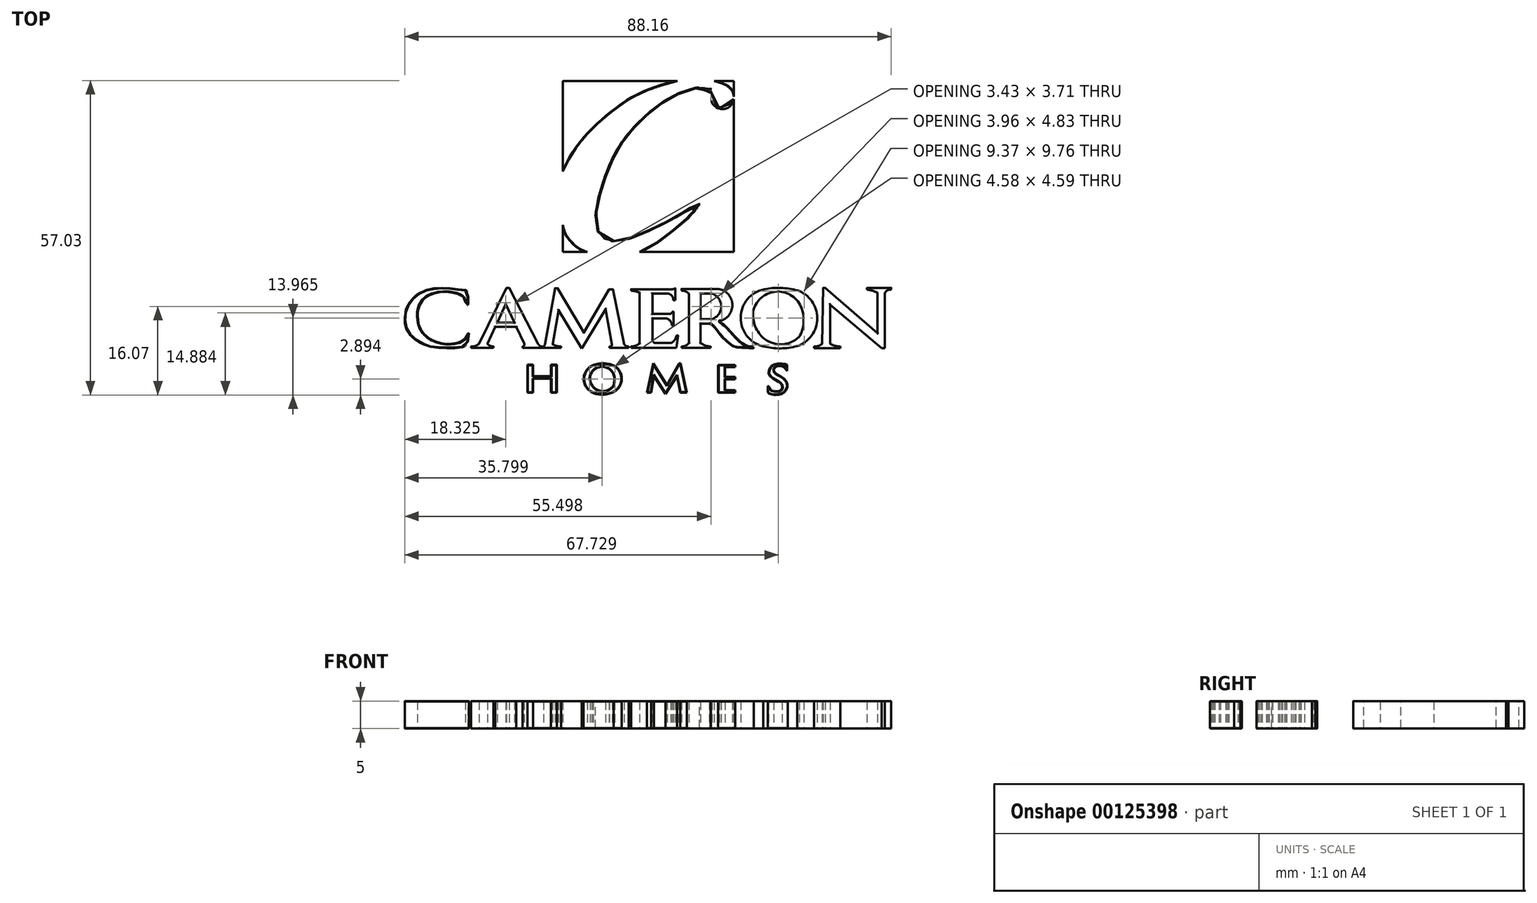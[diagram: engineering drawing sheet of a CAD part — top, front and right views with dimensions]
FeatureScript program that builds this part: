
annotation { "Feature Type Name" : "Feature", "Feature Type Description" : "" }
export const myFeature = defineFeature(function(context is Context, id is Id, definition is map)
    precondition{}
    {
        {
            var Q0;
            Q0=qCreatedBy(makeId("Top.planeOp"),FACE);
            var sketch = newSketch(context, id + "F0", { "sketchPlane" : qUnion([Q0])});
            skLineSegment(sketch, "E0.bottom", {"start": v(-14.52, 26.91) * mm, "end": v(6.23, 26.91) * mm});
            skLineSegment(sketch, "E0.top", {"start": v(-14.52, -4.09) * mm, "end": v(-10.07, -4.09) * mm});
            skLineSegment(sketch, "E0.left", {"start": v(-14.52, 26.91) * mm, "end": v(-14.52, 10.55) * mm});
            skLineSegment(sketch, "E0.right", {"start": v(16.48, 26.91) * mm, "end": v(16.48, -4.09) * mm});
            skFitSpline(sketch, "E1", {"points": [v(-14.52, 10.55) * mm, v(-12.8, 13.8) * mm, v(-10.54, 16.79) * mm, v(-7.6, 19.72) * mm, v(-4.25, 22.4) * mm, v(-1.84, 23.97) * mm, v(0.84, 25.23) * mm, v(3.82, 26.27) * mm, v(6.23, 26.91) * mm], "startDerivative": vector(12.47, 25.45) * mm, "endDerivative": vector(21.85, 5.4) * mm});
            skFitSpline(sketch, "E2", {"points": [v(-14.52, 0.8) * mm, v(-13.95, -0.93) * mm, v(-12.74, -2.45) * mm, v(-11.64, -3.4) * mm, v(-10.07, -4.09) * mm], "startDerivative": vector(1.63, -6.9) * mm, "endDerivative": vector(6.75, -2.5) * mm});
            skFitSpline(sketch, "E3", {"points": [v(-0.63, -4.09) * mm, v(1.88, -2.77) * mm, v(4.5, -0.88) * mm, v(7.18, 1.27) * mm, v(9.12, 3.1) * mm, v(9.91, 3.98) * mm, v(10.2, 4.54) * mm, v(9.82, 4.57) * mm, v(8.32, 3.65) * mm, v(3.94, 1.1) * mm, v(-1.34, -1.28) * mm, v(-4.31, -2.14) * mm, v(-6.9, -1.81) * mm, v(-8.23, -0.28) * mm, v(-8.56, 3.08) * mm, v(-6.57, 10.42) * mm, v(-3.28, 16.62) * mm, v(2, 21.93) * mm, v(6.58, 24.77) * mm, v(10.85, 25.92) * mm, v(12.15, 25.85) * mm, v(12.46, 25.26) * mm, v(12.36, 23.5) * mm, v(12.99, 22.35) * mm, v(14.38, 21.83) * mm, v(15.71, 22.28) * mm, v(16.48, 23.61) * mm, v(16, 25.33) * mm, v(14.84, 26.24) * mm, v(12.92, 26.91) * mm], "startDerivative": vector(70.33, 33.7) * mm, "endDerivative": vector(-67.14, 20.33) * mm});
            skLineSegment(sketch, "E4.trimOffspring", {"start": v(12.92, 26.91) * mm, "end": v(16.48, 26.91) * mm});
            skLineSegment(sketch, "E5.trimOffspring", {"start": v(-14.52, 0.8) * mm, "end": v(-14.52, -4.09) * mm});
            skLineSegment(sketch, "E6.trimOffspring", {"start": v(-0.63, -4.09) * mm, "end": v(16.48, -4.09) * mm});
            skLineSegment(sketch, "E7.bottom", {"start": v(-43.46, -10.36) * mm, "end": v(45.19, -10.36) * mm, "construction": true});
            skLineSegment(sketch, "E7.top", {"start": v(-43.46, -21.79) * mm, "end": v(45.19, -21.79) * mm, "construction": true});
            skLineSegment(sketch, "E7.left", {"start": v(-43.46, -10.36) * mm, "end": v(-43.46, -21.79) * mm, "construction": true});
            skLineSegment(sketch, "E7.right", {"start": v(45.19, -10.36) * mm, "end": v(45.19, -21.79) * mm, "construction": true});
            skPoint(sketch, "E8.23.internal.snap0", {"position": v(-43.46, -16.07) * mm});
            skFitSpline(sketch, "E8", {"points": [v(-33.2, -10.89) * mm, v(-34.84, -10.69) * mm, v(-37.55, -10.64) * mm, v(-40.62, -11.6) * mm, v(-42.6, -13.73) * mm, v(-43.1, -15.32) * mm, v(-43.1, -17.3) * mm, v(-42.36, -18.9) * mm, v(-40.77, -20.32) * mm, v(-38.83, -21.2) * mm, v(-37.55, -21.44) * mm, v(-33.12, -21.47) * mm, v(-32.6, -21.36) * mm, v(-32, -21) * mm, v(-31.53, -19.02) * mm, v(-31.62, -18.87) * mm, v(-31.95, -19.33) * mm, v(-32.42, -19.99) * mm, v(-33.25, -20.45) * mm, v(-34.97, -20.76) * mm, v(-36.91, -20.56) * mm, v(-39.25, -19.4) * mm, v(-40.5, -17.7) * mm, v(-40.81, -16.07) * mm, v(-40.77, -14.52) * mm, v(-39.93, -12.8) * mm, v(-38.57, -11.83) * mm, v(-36.65, -11.37) * mm, v(-34.8, -11.42) * mm, v(-33.32, -11.77) * mm, v(-32.53, -12.28) * mm, v(-32.17, -12.91) * mm, v(-32.1, -13.77) * mm, v(-31.78, -13.84) * mm, v(-31.67, -12.96) * mm, v(-31.69, -11.77) * mm, v(-31.78, -11.13) * mm, v(-33.2, -10.89) * mm]});
            skLineSegment(sketch, "E9", {"start": v(-29.73, -20.74) * mm, "end": v(-24.72, -10.6) * mm});
            skLineSegment(sketch, "E10", {"start": v(-24.72, -10.6) * mm, "end": v(-24.26, -10.6) * mm});
            skLineSegment(sketch, "E11", {"start": v(-24.26, -10.6) * mm, "end": v(-19.04, -20.74) * mm});
            skLineSegment(sketch, "E12", {"start": v(-21.54, -20.74) * mm, "end": v(-24.86, -13.52) * mm});
            skLineSegment(sketch, "E13", {"start": v(-24.86, -13.52) * mm, "end": v(-28.2, -20.7) * mm});
            skLineSegment(sketch, "E14", {"start": v(-26.42, -16.9) * mm, "end": v(-23.3, -16.9) * mm});
            skLineSegment(sketch, "E15", {"start": v(-26.78, -17.66) * mm, "end": v(-22.95, -17.66) * mm});
            skLineSegment(sketch, "E16", {"start": v(-31.15, -21.24) * mm, "end": v(-31.15, -21.49) * mm});
            skLineSegment(sketch, "E17", {"start": v(-31.15, -21.49) * mm, "end": v(-27.07, -21.49) * mm});
            skLineSegment(sketch, "E18", {"start": v(-27.07, -21.49) * mm, "end": v(-27.07, -21.24) * mm});
            skLineSegment(sketch, "E19", {"start": v(-21.83, -21.24) * mm, "end": v(-21.83, -21.49) * mm});
            skLineSegment(sketch, "E20", {"start": v(-21.83, -21.49) * mm, "end": v(-18, -21.49) * mm});
            skLineSegment(sketch, "E21", {"start": v(-18, -21.49) * mm, "end": v(-18, -21.24) * mm});
            skArc(sketch, "E22", {"start": v(-31.15, -21.24) * mm, "mid": v(-30.38, -21.14) * mm, "end": v(-29.73, -20.74) * mm});
            skArc(sketch, "E23", {"start": v(-28.2, -20.7) * mm, "mid": v(-27.7, -21.1) * mm, "end": v(-27.07, -21.24) * mm});
            skArc(sketch, "E24", {"start": v(-21.83, -21.24) * mm, "mid": v(-21.55, -21.06) * mm, "end": v(-21.54, -20.74) * mm});
            skArc(sketch, "E25", {"start": v(-19.04, -20.74) * mm, "mid": v(-18.6, -21.16) * mm, "end": v(-18, -21.24) * mm});
            skLineSegment(sketch, "E26", {"start": v(-17.78, -20.8) * mm, "end": v(-15.93, -10.65) * mm});
            skLineSegment(sketch, "E27", {"start": v(-15.93, -10.65) * mm, "end": v(-15.45, -10.65) * mm});
            skLineSegment(sketch, "E28", {"start": v(-15.45, -10.65) * mm, "end": v(-10.72, -18.68) * mm});
            skLineSegment(sketch, "E29", {"start": v(-10.72, -18.68) * mm, "end": v(-6.12, -10.86) * mm});
            skLineSegment(sketch, "E30", {"start": v(-6.12, -10.86) * mm, "end": v(-5.47, -10.86) * mm});
            skLineSegment(sketch, "E31", {"start": v(-5.47, -10.86) * mm, "end": v(-3.4, -20.8) * mm});
            skLineSegment(sketch, "E32", {"start": v(-16.38, -20.8) * mm, "end": v(-15.3, -14.7) * mm});
            skLineSegment(sketch, "E33", {"start": v(-15.3, -14.7) * mm, "end": v(-11.1, -21.58) * mm});
            skLineSegment(sketch, "E34", {"start": v(-11.1, -21.58) * mm, "end": v(-6.78, -14.48) * mm});
            skLineSegment(sketch, "E35", {"start": v(-6.78, -14.48) * mm, "end": v(-5.61, -20.8) * mm});
            skLineSegment(sketch, "E36", {"start": v(-18, -21.49) * mm, "end": v(-14.86, -21.49) * mm});
            skLineSegment(sketch, "E37", {"start": v(-14.86, -21.49) * mm, "end": v(-14.86, -21.24) * mm});
            skLineSegment(sketch, "E38", {"start": v(-6.05, -21.49) * mm, "end": v(-2.6, -21.49) * mm});
            skLineSegment(sketch, "E39", {"start": v(-2.6, -21.49) * mm, "end": v(-2.6, -21.24) * mm});
            skLineSegment(sketch, "E40", {"start": v(-6.05, -21.49) * mm, "end": v(-6.05, -21.24) * mm});
            skArc(sketch, "E41", {"start": v(-18, -21.24) * mm, "mid": v(-17.86, -21.04) * mm, "end": v(-17.78, -20.8) * mm});
            skArc(sketch, "E42", {"start": v(-16.38, -20.8) * mm, "mid": v(-15.65, -21.13) * mm, "end": v(-14.86, -21.24) * mm});
            skArc(sketch, "E43", {"start": v(-6.05, -21.24) * mm, "mid": v(-5.72, -21.14) * mm, "end": v(-5.61, -20.8) * mm});
            skArc(sketch, "E44", {"start": v(-3.4, -20.8) * mm, "mid": v(-3.05, -21.13) * mm, "end": v(-2.6, -21.24) * mm});
            skLineSegment(sketch, "E45", {"start": v(-2.16, -10.85) * mm, "end": v(5.22, -10.85) * mm});
            skLineSegment(sketch, "E46", {"start": v(-0.62, -11.48) * mm, "end": v(-0.62, -20.66) * mm});
            skLineSegment(sketch, "E47", {"start": v(4.35, -11.62) * mm, "end": v(1.71, -11.62) * mm});
            skLineSegment(sketch, "E48", {"start": v(1.71, -11.62) * mm, "end": v(1.71, -15.31) * mm});
            skLineSegment(sketch, "E49", {"start": v(1.71, -15.31) * mm, "end": v(4.87, -15.31) * mm});
            skLineSegment(sketch, "E50", {"start": v(4.4, -16.15) * mm, "end": v(1.71, -16.15) * mm});
            skLineSegment(sketch, "E51", {"start": v(1.71, -16.15) * mm, "end": v(1.71, -19.82) * mm});
            skLineSegment(sketch, "E52", {"start": v(2.32, -20.61) * mm, "end": v(5.03, -20.61) * mm});
            skLineSegment(sketch, "E53", {"start": v(5.85, -10.66) * mm, "end": v(5.85, -12.86) * mm});
            skLineSegment(sketch, "E54", {"start": v(5.54, -14.96) * mm, "end": v(5.54, -17.39) * mm});
            skLineSegment(sketch, "E55", {"start": v(6.38, -19.28) * mm, "end": v(6.07, -21.49) * mm});
            skLineSegment(sketch, "E56", {"start": v(6.07, -21.49) * mm, "end": v(-2.16, -21.49) * mm});
            skLineSegment(sketch, "E57", {"start": v(-2.16, -21.49) * mm, "end": v(-2.16, -21.24) * mm});
            skLineSegment(sketch, "E58", {"start": v(-2.16, -10.85) * mm, "end": v(-2.16, -11.13) * mm});
            skLineSegment(sketch, "E59", {"start": v(5.85, -12.86) * mm, "end": v(5.5, -12.86) * mm});
            skLineSegment(sketch, "E60", {"start": v(5.54, -14.96) * mm, "end": v(5.3, -14.96) * mm});
            skLineSegment(sketch, "E61", {"start": v(5.54, -17.39) * mm, "end": v(5.25, -17.39) * mm});
            skLineSegment(sketch, "E62", {"start": v(6.38, -19.28) * mm, "end": v(6.05, -19.28) * mm});
            skArc(sketch, "E63", {"start": v(-0.62, -11.48) * mm, "mid": v(-1.37, -11.21) * mm, "end": v(-2.16, -11.13) * mm});
            skArc(sketch, "E64", {"start": v(-2.16, -21.24) * mm, "mid": v(-1.34, -21.09) * mm, "end": v(-0.62, -20.66) * mm});
            skArc(sketch, "E65", {"start": v(5.5, -12.86) * mm, "mid": v(5.2, -12) * mm, "end": v(4.35, -11.62) * mm});
            skArc(sketch, "E66", {"start": v(5.25, -17.39) * mm, "mid": v(5, -16.65) * mm, "end": v(4.4, -16.15) * mm});
            skArc(sketch, "E67", {"start": v(5.03, -20.61) * mm, "mid": v(5.71, -20.08) * mm, "end": v(6.05, -19.28) * mm});
            skArc(sketch, "E68", {"start": v(1.71, -19.82) * mm, "mid": v(1.82, -20.36) * mm, "end": v(2.32, -20.61) * mm});
            skArc(sketch, "E69", {"start": v(4.87, -15.31) * mm, "mid": v(5.14, -15.21) * mm, "end": v(5.3, -14.96) * mm});
            skArc(sketch, "E70", {"start": v(5.22, -10.85) * mm, "mid": v(5.55, -10.8) * mm, "end": v(5.85, -10.66) * mm});
            skLineSegment(sketch, "E71", {"start": v(6.97, -10.8) * mm, "end": v(13.74, -10.8) * mm});
            skPoint(sketch, "E71.startSnap0", {"position": v(5.55, -10.8) * mm});
            skLineSegment(sketch, "E72", {"start": v(10.43, -11.64) * mm, "end": v(10.43, -16.26) * mm});
            skLineSegment(sketch, "E73", {"start": v(10.43, -16.26) * mm, "end": v(12.5, -16.26) * mm});
            skLineSegment(sketch, "E74", {"start": v(8.36, -11.7) * mm, "end": v(8.36, -20.58) * mm});
            skLineSegment(sketch, "E75", {"start": v(12.04, -17.1) * mm, "end": v(10.43, -17.1) * mm});
            skLineSegment(sketch, "E76", {"start": v(10.43, -17.1) * mm, "end": v(10.43, -20.58) * mm});
            skLineSegment(sketch, "E77", {"start": v(7.01, -21.49) * mm, "end": v(12.26, -21.49) * mm});
            skLineSegment(sketch, "E78", {"start": v(12.26, -21.49) * mm, "end": v(12.26, -21.24) * mm});
            skLineSegment(sketch, "E79", {"start": v(7.01, -21.49) * mm, "end": v(7.01, -21.24) * mm});
            skArc(sketch, "E80", {"start": v(7.01, -21.24) * mm, "mid": v(7.76, -21.07) * mm, "end": v(8.36, -20.58) * mm});
            skArc(sketch, "E81", {"start": v(10.43, -20.58) * mm, "mid": v(11.3, -21.05) * mm, "end": v(12.26, -21.24) * mm});
            skLineSegment(sketch, "E82", {"start": v(6.97, -10.8) * mm, "end": v(6.97, -11.1) * mm});
            skArc(sketch, "E83", {"start": v(8.36, -11.7) * mm, "mid": v(7.74, -11.23) * mm, "end": v(6.97, -11.1) * mm});
            skLineSegment(sketch, "E84", {"start": v(10.43, -11.64) * mm, "end": v(12.5, -11.64) * mm});
            skArc(sketch, "E85", {"start": v(12.5, -16.26) * mm, "mid": v(14.19, -13.95) * mm, "end": v(12.5, -11.64) * mm});
            skArc(sketch, "E86", {"start": v(14.19, -16.53) * mm, "mid": v(16.2, -13.5) * mm, "end": v(13.74, -10.8) * mm});
            skPoint(sketch, "E86.startSnap0", {"position": v(14.19, -13.95) * mm});
            skFitSpline(sketch, "E87", {"points": [v(12.04, -17.1) * mm, v(12.53, -17.33) * mm, v(14.14, -19.28) * mm, v(15.87, -20.92) * mm, v(16.89, -21.36) * mm, v(19.98, -21.53) * mm, v(20.07, -21.51) * mm, v(19.9, -21.27) * mm, v(19.44, -21.22) * mm, v(17.87, -20.52) * mm, v(15.92, -18.58) * mm, v(14.4, -17.1) * mm, v(13.83, -16.63) * mm, v(14.19, -16.53) * mm], "startDerivative": vector(8.71, -2.21) * mm, "endDerivative": vector(12, 1.45) * mm});
            skArc(sketch, "E88", {"start": v(27.94, -21.15) * mm, "mid": v(31.58, -16.12) * mm, "end": v(27.99, -11.06) * mm});
            skArc(sketch, "E89", {"start": v(21.93, -10.86) * mm, "mid": v(17.7, -15.98) * mm, "end": v(21.8, -21.2) * mm});
            skArc(sketch, "E90", {"start": v(27.99, -11.06) * mm, "mid": v(24.97, -10.6) * mm, "end": v(21.93, -10.86) * mm});
            skArc(sketch, "E91", {"start": v(21.8, -21.2) * mm, "mid": v(24.87, -21.57) * mm, "end": v(27.94, -21.15) * mm});
            skArc(sketch, "E92", {"start": v(28.76, -14.32) * mm, "mid": v(24.28, -11.27) * mm, "end": v(20.02, -14.62) * mm});
            skArc(sketch, "E93", {"start": v(21.68, -19.57) * mm, "mid": v(25.03, -20.84) * mm, "end": v(28.33, -19.47) * mm});
            skArc(sketch, "E94", {"start": v(28.33, -19.47) * mm, "mid": v(29.1, -16.94) * mm, "end": v(28.76, -14.32) * mm});
            skArc(sketch, "E95", {"start": v(20.02, -14.62) * mm, "mid": v(20.24, -17.3) * mm, "end": v(21.68, -19.57) * mm});
            skLineSegment(sketch, "E96", {"start": v(32.45, -20.73) * mm, "end": v(32.66, -10.58) * mm});
            skLineSegment(sketch, "E97", {"start": v(32.66, -10.58) * mm, "end": v(33.06, -10.59) * mm});
            skLineSegment(sketch, "E98", {"start": v(33.06, -10.59) * mm, "end": v(42.5, -18.77) * mm});
            skLineSegment(sketch, "E99", {"start": v(42.5, -18.77) * mm, "end": v(42.5, -11.53) * mm});
            skLineSegment(sketch, "E100", {"start": v(43.85, -11.53) * mm, "end": v(43.85, -21.56) * mm});
            skLineSegment(sketch, "E101", {"start": v(43.85, -21.56) * mm, "end": v(43.23, -21.56) * mm});
            skLineSegment(sketch, "E102", {"start": v(43.23, -21.56) * mm, "end": v(33.93, -13.64) * mm});
            skLineSegment(sketch, "E103", {"start": v(33.93, -13.64) * mm, "end": v(33.93, -20.73) * mm});
            skLineSegment(sketch, "E104", {"start": v(31.03, -21.24) * mm, "end": v(31.03, -21.51) * mm});
            skLineSegment(sketch, "E105", {"start": v(31.03, -21.51) * mm, "end": v(35.76, -21.51) * mm});
            skLineSegment(sketch, "E106", {"start": v(35.76, -21.51) * mm, "end": v(35.76, -21.24) * mm});
            skLineSegment(sketch, "E107", {"start": v(40.6, -10.59) * mm, "end": v(44.97, -10.59) * mm});
            skLineSegment(sketch, "E108", {"start": v(44.97, -10.59) * mm, "end": v(44.97, -10.95) * mm});
            skLineSegment(sketch, "E109", {"start": v(40.6, -10.59) * mm, "end": v(40.6, -10.95) * mm});
            skArc(sketch, "E110", {"start": v(31.03, -21.24) * mm, "mid": v(31.8, -21.13) * mm, "end": v(32.45, -20.73) * mm});
            skArc(sketch, "E111", {"start": v(33.93, -20.73) * mm, "mid": v(34.81, -21.1) * mm, "end": v(35.76, -21.24) * mm});
            skArc(sketch, "E112", {"start": v(42.5, -11.53) * mm, "mid": v(41.6, -11.1) * mm, "end": v(40.6, -10.95) * mm});
            skArc(sketch, "E113", {"start": v(44.97, -10.95) * mm, "mid": v(44.31, -11.04) * mm, "end": v(43.85, -11.53) * mm});
            skLineSegment(sketch, "E114.bottom", {"start": v(-20.97, -24.52) * mm, "end": v(-19.92, -24.52) * mm});
            skLineSegment(sketch, "E114.top", {"start": v(-20.97, -29.63) * mm, "end": v(-19.92, -29.63) * mm});
            skLineSegment(sketch, "E114.left", {"start": v(-20.97, -24.52) * mm, "end": v(-20.97, -29.63) * mm});
            skLineSegment(sketch, "E114.right", {"start": v(-19.92, -24.52) * mm, "end": v(-19.92, -29.63) * mm});
            skLineSegment(sketch, "E115.bottom", {"start": v(-16.67, -24.52) * mm, "end": v(-15.62, -24.52) * mm});
            skLineSegment(sketch, "E115.top", {"start": v(-16.67, -29.63) * mm, "end": v(-15.62, -29.63) * mm});
            skLineSegment(sketch, "E115.left", {"start": v(-16.67, -24.52) * mm, "end": v(-16.67, -29.63) * mm});
            skLineSegment(sketch, "E115.right", {"start": v(-15.62, -24.52) * mm, "end": v(-15.62, -29.63) * mm});
            skLineSegment(sketch, "E116.bottom", {"start": v(-19.92, -26.64) * mm, "end": v(-16.67, -26.64) * mm});
            skLineSegment(sketch, "E116.top", {"start": v(-19.92, -27.07) * mm, "end": v(-16.67, -27.07) * mm});
            skLineSegment(sketch, "E116.left", {"start": v(-19.92, -26.64) * mm, "end": v(-19.92, -27.07) * mm});
            skLineSegment(sketch, "E116.right", {"start": v(-16.67, -26.64) * mm, "end": v(-16.67, -27.07) * mm});
            skArc(sketch, "E117", {"start": v(-5.2, -27) * mm, "mid": v(-7.2, -24.93) * mm, "end": v(-9.55, -26.6) * mm});
            skArc(sketch, "E118", {"start": v(-9.28, -28.1) * mm, "mid": v(-7.34, -29.32) * mm, "end": v(-5.33, -28.23) * mm});
            skArc(sketch, "E119", {"start": v(-5.33, -28.23) * mm, "mid": v(-5.23, -27.62) * mm, "end": v(-5.2, -27) * mm});
            skArc(sketch, "E120", {"start": v(-9.55, -26.6) * mm, "mid": v(-9.55, -27.38) * mm, "end": v(-9.28, -28.1) * mm});
            skArc(sketch, "E121", {"start": v(-9.02, -24.57) * mm, "mid": v(-10.75, -27.16) * mm, "end": v(-8.93, -29.7) * mm});
            skArc(sketch, "E122", {"start": v(-5.33, -29.5) * mm, "mid": v(-3.84, -27.18) * mm, "end": v(-5.12, -24.75) * mm});
            skArc(sketch, "E123", {"start": v(-5.12, -24.75) * mm, "mid": v(-7.05, -24.29) * mm, "end": v(-9.02, -24.57) * mm});
            skArc(sketch, "E124", {"start": v(-8.93, -29.7) * mm, "mid": v(-7.1, -29.96) * mm, "end": v(-5.33, -29.5) * mm});
            skLineSegment(sketch, "E125", {"start": v(1.86, -24.29) * mm, "end": v(4.32, -28.22) * mm});
            skLineSegment(sketch, "E126", {"start": v(4.32, -28.22) * mm, "end": v(6.57, -24.29) * mm});
            skLineSegment(sketch, "E127", {"start": v(6.57, -24.29) * mm, "end": v(6.8, -24.29) * mm});
            skLineSegment(sketch, "E128", {"start": v(6.8, -24.29) * mm, "end": v(7.94, -29.57) * mm});
            skLineSegment(sketch, "E129", {"start": v(7.94, -29.57) * mm, "end": v(6.72, -29.57) * mm});
            skLineSegment(sketch, "E130", {"start": v(6.72, -29.57) * mm, "end": v(6.14, -26.64) * mm});
            skLineSegment(sketch, "E131", {"start": v(6.14, -26.64) * mm, "end": v(4.1, -29.89) * mm});
            skLineSegment(sketch, "E132", {"start": v(4.1, -29.89) * mm, "end": v(1.99, -26.59) * mm});
            skLineSegment(sketch, "E133", {"start": v(1.99, -26.59) * mm, "end": v(1.5, -29.57) * mm});
            skLineSegment(sketch, "E134", {"start": v(1.5, -29.57) * mm, "end": v(0.71, -29.57) * mm});
            skLineSegment(sketch, "E135", {"start": v(0.71, -29.57) * mm, "end": v(1.86, -24.29) * mm});
            skLineSegment(sketch, "E136.bottom", {"start": v(13.62, -24.57) * mm, "end": v(14.88, -24.57) * mm});
            skLineSegment(sketch, "E136.top", {"start": v(13.62, -29.63) * mm, "end": v(14.88, -29.63) * mm});
            skLineSegment(sketch, "E136.left", {"start": v(13.62, -24.57) * mm, "end": v(13.62, -29.63) * mm});
            skLineSegment(sketch, "E136.right", {"start": v(14.88, -24.57) * mm, "end": v(14.88, -29.63) * mm});
            skLineSegment(sketch, "E137.bottom", {"start": v(14.88, -24.57) * mm, "end": v(16.7, -24.57) * mm});
            skLineSegment(sketch, "E137.top", {"start": v(14.88, -24.97) * mm, "end": v(16.7, -24.97) * mm});
            skLineSegment(sketch, "E137.left", {"start": v(14.88, -24.57) * mm, "end": v(14.88, -24.97) * mm});
            skLineSegment(sketch, "E137.right", {"start": v(16.7, -24.57) * mm, "end": v(16.7, -24.97) * mm});
            skLineSegment(sketch, "E138.bottom", {"start": v(14.88, -26.76) * mm, "end": v(16.7, -26.76) * mm});
            skLineSegment(sketch, "E138.top", {"start": v(14.88, -27.16) * mm, "end": v(16.7, -27.16) * mm});
            skLineSegment(sketch, "E138.left", {"start": v(14.88, -26.76) * mm, "end": v(14.88, -27.16) * mm});
            skLineSegment(sketch, "E138.right", {"start": v(16.7, -26.76) * mm, "end": v(16.7, -27.16) * mm});
            skLineSegment(sketch, "E139.bottom", {"start": v(14.88, -29.63) * mm, "end": v(16.7, -29.63) * mm});
            skLineSegment(sketch, "E139.top", {"start": v(14.88, -29.15) * mm, "end": v(16.7, -29.15) * mm});
            skLineSegment(sketch, "E139.left", {"start": v(14.88, -29.63) * mm, "end": v(14.88, -29.15) * mm});
            skLineSegment(sketch, "E139.right", {"start": v(16.7, -29.63) * mm, "end": v(16.7, -29.15) * mm});
            skLineSegment(sketch, "E140", {"start": v(22.6, -28.37) * mm, "end": v(22.6, -29.54) * mm});
            skLineSegment(sketch, "E141", {"start": v(26.13, -24.51) * mm, "end": v(26.13, -25.65) * mm});
            skFitSpline(sketch, "E142", {"points": [v(26.13, -24.51) * mm, v(25.52, -24.37) * mm, v(24.08, -24.35) * mm, v(23.24, -24.8) * mm, v(22.8, -25.57) * mm, v(22.86, -26.37) * mm, v(23.68, -27.12) * mm, v(24.64, -27.69) * mm, v(25.14, -28.16) * mm, v(25.23, -28.73) * mm, v(25.05, -29.18) * mm, v(24.46, -29.34) * mm, v(23.71, -29.3) * mm, v(23.17, -29.09) * mm, v(22.9, -28.6) * mm, v(22.6, -28.37) * mm], "startDerivative": vector(-8.49, 2.6) * mm, "endDerivative": vector(-7.14, 3.76) * mm});
            skFitSpline(sketch, "E143", {"points": [v(22.6, -29.54) * mm, v(22.86, -29.78) * mm, v(23.85, -30.01) * mm, v(25, -29.88) * mm, v(25.82, -29.34) * mm, v(26.2, -28.43) * mm, v(26.02, -27.59) * mm, v(25.07, -26.67) * mm, v(24.07, -26.09) * mm, v(23.71, -25.65) * mm, v(23.77, -25.25) * mm, v(24.08, -24.9) * mm, v(24.71, -24.8) * mm, v(25.42, -24.9) * mm, v(25.76, -25.22) * mm, v(26.13, -25.65) * mm], "startDerivative": vector(4.46, -5.37) * mm, "endDerivative": vector(6.63, -7.42) * mm});
            skSolve(sketch);
        }
        {
            var Q0;
            Q0 = qSketchRegion(id + "F0", true);
            extrude(context, id + "F1", {"entities" : qUnion([Q0]), "depth" : 5 * mm});
        }
        {
            var Q0;
            Q0=makeQuery(id+"F1.opExtrude","CAP_FACE",FACE,{"disambiguationData":[OSD([sQuery(id+"F0.wireOp",EDGE,"E0.right"),sQuery(id+"F0.wireOp",EDGE,"E3"),sQuery(id+"F0.wireOp",EDGE,"E6.trimOffspring")])],"isStart":false});
            var Q1;
            Q1=makeQuery(id+"F1.opExtrude","CAP_FACE",FACE,{"disambiguationData":[OSD([sQuery(id+"F0.wireOp",EDGE,"E0.bottom"),sQuery(id+"F0.wireOp",EDGE,"E0.left"),sQuery(id+"F0.wireOp",EDGE,"E1")])],"isStart":false});
            var Q2;
            {var subQ0=sQuery(id+"F0.wireOp",EDGE,"E3");Q2=makeQuery(id+"F1.opExtrude","CAP_EDGE",EDGE,{"disambiguationData":[OSD([subQ0]),TDD([makeQuery(id+"F0.imprint","IMPRINT",EDGE,{"disambiguationData":[TD([[makeQuery(id+"F0.imprint","INTERSECT",VERTEX,{"derivedFrom":[subQ0,sQuery(id+"F0.wireOp",EDGE,"E4.trimOffspring")]}),1.0]])],"derivedFrom":subQ0})])],"isStart":false});}
            var Q3;
            Q3=makeQuery(id+"F1.opExtrude","CAP_FACE",FACE,{"disambiguationData":[OSD([sQuery(id+"F0.wireOp",EDGE,"E0.top"),sQuery(id+"F0.wireOp",EDGE,"E2"),sQuery(id+"F0.wireOp",EDGE,"E5.trimOffspring")])],"isStart":false});
            var Q4;
            Q4=makeQuery(id+"F1.opExtrude","CAP_FACE",FACE,{"disambiguationData":[OSD([sQuery(id+"F0.wireOp",EDGE,"E8")])],"isStart":false});
            var Q5;
            Q5=makeQuery(id+"F1.opExtrude","CAP_FACE",FACE,{"disambiguationData":[OSD([sQuery(id+"F0.wireOp",EDGE,"E9"),sQuery(id+"F0.wireOp",EDGE,"E10"),sQuery(id+"F0.wireOp",EDGE,"E11"),sQuery(id+"F0.wireOp",EDGE,"E12"),sQuery(id+"F0.wireOp",EDGE,"E13"),sQuery(id+"F0.wireOp",EDGE,"E14"),sQuery(id+"F0.wireOp",EDGE,"E15"),sQuery(id+"F0.wireOp",EDGE,"E16"),sQuery(id+"F0.wireOp",EDGE,"E17"),sQuery(id+"F0.wireOp",EDGE,"E18"),sQuery(id+"F0.wireOp",EDGE,"E19"),sQuery(id+"F0.wireOp",EDGE,"E20"),sQuery(id+"F0.wireOp",EDGE,"E22"),sQuery(id+"F0.wireOp",EDGE,"E23"),sQuery(id+"F0.wireOp",EDGE,"E24"),sQuery(id+"F0.wireOp",EDGE,"E25"),sQuery(id+"F0.wireOp",EDGE,"E26"),sQuery(id+"F0.wireOp",EDGE,"E27"),sQuery(id+"F0.wireOp",EDGE,"E28"),sQuery(id+"F0.wireOp",EDGE,"E29"),sQuery(id+"F0.wireOp",EDGE,"E30"),sQuery(id+"F0.wireOp",EDGE,"E31"),sQuery(id+"F0.wireOp",EDGE,"E32"),sQuery(id+"F0.wireOp",EDGE,"E33"),sQuery(id+"F0.wireOp",EDGE,"E34"),sQuery(id+"F0.wireOp",EDGE,"E35"),sQuery(id+"F0.wireOp",EDGE,"E36"),sQuery(id+"F0.wireOp",EDGE,"E37"),sQuery(id+"F0.wireOp",EDGE,"E38"),sQuery(id+"F0.wireOp",EDGE,"E39"),sQuery(id+"F0.wireOp",EDGE,"E40"),sQuery(id+"F0.wireOp",EDGE,"E41"),sQuery(id+"F0.wireOp",EDGE,"E42"),sQuery(id+"F0.wireOp",EDGE,"E43"),sQuery(id+"F0.wireOp",EDGE,"E44")])],"isStart":false});
            var Q6;
            Q6=makeQuery(id+"F1.opExtrude","CAP_FACE",FACE,{"disambiguationData":[OSD([sQuery(id+"F0.wireOp",EDGE,"E45"),sQuery(id+"F0.wireOp",EDGE,"E46"),sQuery(id+"F0.wireOp",EDGE,"E47"),sQuery(id+"F0.wireOp",EDGE,"E48"),sQuery(id+"F0.wireOp",EDGE,"E49"),sQuery(id+"F0.wireOp",EDGE,"E50"),sQuery(id+"F0.wireOp",EDGE,"E51"),sQuery(id+"F0.wireOp",EDGE,"E52"),sQuery(id+"F0.wireOp",EDGE,"E53"),sQuery(id+"F0.wireOp",EDGE,"E54"),sQuery(id+"F0.wireOp",EDGE,"E55"),sQuery(id+"F0.wireOp",EDGE,"E56"),sQuery(id+"F0.wireOp",EDGE,"E57"),sQuery(id+"F0.wireOp",EDGE,"E58"),sQuery(id+"F0.wireOp",EDGE,"E59"),sQuery(id+"F0.wireOp",EDGE,"E60"),sQuery(id+"F0.wireOp",EDGE,"E61"),sQuery(id+"F0.wireOp",EDGE,"E62"),sQuery(id+"F0.wireOp",EDGE,"E63"),sQuery(id+"F0.wireOp",EDGE,"E64"),sQuery(id+"F0.wireOp",EDGE,"E65"),sQuery(id+"F0.wireOp",EDGE,"E66"),sQuery(id+"F0.wireOp",EDGE,"E67"),sQuery(id+"F0.wireOp",EDGE,"E68"),sQuery(id+"F0.wireOp",EDGE,"E69"),sQuery(id+"F0.wireOp",EDGE,"E70")])],"isStart":false});
            var Q7;
            Q7=makeQuery(id+"F1.opExtrude","CAP_FACE",FACE,{"disambiguationData":[OSD([sQuery(id+"F0.wireOp",EDGE,"E71"),sQuery(id+"F0.wireOp",EDGE,"E72"),sQuery(id+"F0.wireOp",EDGE,"E73"),sQuery(id+"F0.wireOp",EDGE,"E74"),sQuery(id+"F0.wireOp",EDGE,"E75"),sQuery(id+"F0.wireOp",EDGE,"E76"),sQuery(id+"F0.wireOp",EDGE,"E77"),sQuery(id+"F0.wireOp",EDGE,"E78"),sQuery(id+"F0.wireOp",EDGE,"E79"),sQuery(id+"F0.wireOp",EDGE,"E80"),sQuery(id+"F0.wireOp",EDGE,"E81"),sQuery(id+"F0.wireOp",EDGE,"E82"),sQuery(id+"F0.wireOp",EDGE,"E83"),sQuery(id+"F0.wireOp",EDGE,"E84"),sQuery(id+"F0.wireOp",EDGE,"E85"),sQuery(id+"F0.wireOp",EDGE,"E86"),sQuery(id+"F0.wireOp",EDGE,"E87")])],"isStart":false});
            var Q8;
            Q8=makeQuery(id+"F1.opExtrude","CAP_FACE",FACE,{"disambiguationData":[OSD([sQuery(id+"F0.wireOp",EDGE,"E88"),sQuery(id+"F0.wireOp",EDGE,"E89"),sQuery(id+"F0.wireOp",EDGE,"E90"),sQuery(id+"F0.wireOp",EDGE,"E91"),sQuery(id+"F0.wireOp",EDGE,"E92"),sQuery(id+"F0.wireOp",EDGE,"E93"),sQuery(id+"F0.wireOp",EDGE,"E94"),sQuery(id+"F0.wireOp",EDGE,"E95")])],"isStart":false});
            var Q9;
            Q9=makeQuery(id+"F1.opExtrude","CAP_FACE",FACE,{"disambiguationData":[OSD([sQuery(id+"F0.wireOp",EDGE,"E96"),sQuery(id+"F0.wireOp",EDGE,"E97"),sQuery(id+"F0.wireOp",EDGE,"E98"),sQuery(id+"F0.wireOp",EDGE,"E99"),sQuery(id+"F0.wireOp",EDGE,"E100"),sQuery(id+"F0.wireOp",EDGE,"E101"),sQuery(id+"F0.wireOp",EDGE,"E102"),sQuery(id+"F0.wireOp",EDGE,"E103"),sQuery(id+"F0.wireOp",EDGE,"E104"),sQuery(id+"F0.wireOp",EDGE,"E105"),sQuery(id+"F0.wireOp",EDGE,"E106"),sQuery(id+"F0.wireOp",EDGE,"E107"),sQuery(id+"F0.wireOp",EDGE,"E108"),sQuery(id+"F0.wireOp",EDGE,"E109"),sQuery(id+"F0.wireOp",EDGE,"E110"),sQuery(id+"F0.wireOp",EDGE,"E111"),sQuery(id+"F0.wireOp",EDGE,"E112"),sQuery(id+"F0.wireOp",EDGE,"E113")])],"isStart":false});
            fillet(context, id + "F2", {"entities" : qUnion([Q0, Q1, Q2, Q3, Q4, Q5, Q6, Q7, Q8, Q9]), "radius" : .1 * mm, "tangentPropagation" : true, "allowEdgeOverflow" : false});
        }
        {
            var Q0;
            Q0=makeQuery(id+"F1.opExtrude","CAP_FACE",FACE,{"disambiguationData":[OSD([sQuery(id+"F0.wireOp",EDGE,"E114.bottom"),sQuery(id+"F0.wireOp",EDGE,"E114.top"),sQuery(id+"F0.wireOp",EDGE,"E114.left"),sQuery(id+"F0.wireOp",EDGE,"E114.right"),sQuery(id+"F0.wireOp",EDGE,"E115.bottom"),sQuery(id+"F0.wireOp",EDGE,"E115.top"),sQuery(id+"F0.wireOp",EDGE,"E115.left"),sQuery(id+"F0.wireOp",EDGE,"E115.right"),sQuery(id+"F0.wireOp",EDGE,"E116.bottom"),sQuery(id+"F0.wireOp",EDGE,"E116.top")])],"isStart":false});
            var Q1;
            Q1=makeQuery(id+"F1.opExtrude","CAP_FACE",FACE,{"disambiguationData":[OSD([sQuery(id+"F0.wireOp",EDGE,"E117"),sQuery(id+"F0.wireOp",EDGE,"E118"),sQuery(id+"F0.wireOp",EDGE,"E119"),sQuery(id+"F0.wireOp",EDGE,"E120"),sQuery(id+"F0.wireOp",EDGE,"E121"),sQuery(id+"F0.wireOp",EDGE,"E122"),sQuery(id+"F0.wireOp",EDGE,"E123"),sQuery(id+"F0.wireOp",EDGE,"E124")])],"isStart":false});
            var Q2;
            Q2=makeQuery(id+"F1.opExtrude","CAP_FACE",FACE,{"disambiguationData":[OSD([sQuery(id+"F0.wireOp",EDGE,"E125"),sQuery(id+"F0.wireOp",EDGE,"E126"),sQuery(id+"F0.wireOp",EDGE,"E127"),sQuery(id+"F0.wireOp",EDGE,"E128"),sQuery(id+"F0.wireOp",EDGE,"E129"),sQuery(id+"F0.wireOp",EDGE,"E130"),sQuery(id+"F0.wireOp",EDGE,"E131"),sQuery(id+"F0.wireOp",EDGE,"E132"),sQuery(id+"F0.wireOp",EDGE,"E133"),sQuery(id+"F0.wireOp",EDGE,"E134"),sQuery(id+"F0.wireOp",EDGE,"E135")])],"isStart":false});
            var Q3;
            Q3=makeQuery(id+"F1.opExtrude","CAP_FACE",FACE,{"disambiguationData":[OSD([sQuery(id+"F0.wireOp",EDGE,"E136.bottom"),sQuery(id+"F0.wireOp",EDGE,"E136.top"),sQuery(id+"F0.wireOp",EDGE,"E136.left"),sQuery(id+"F0.wireOp",EDGE,"E136.right"),sQuery(id+"F0.wireOp",EDGE,"E137.bottom"),sQuery(id+"F0.wireOp",EDGE,"E137.top"),sQuery(id+"F0.wireOp",EDGE,"E137.right"),sQuery(id+"F0.wireOp",EDGE,"E138.bottom"),sQuery(id+"F0.wireOp",EDGE,"E138.top"),sQuery(id+"F0.wireOp",EDGE,"E138.right"),sQuery(id+"F0.wireOp",EDGE,"E139.bottom"),sQuery(id+"F0.wireOp",EDGE,"E139.top"),sQuery(id+"F0.wireOp",EDGE,"E139.right")])],"isStart":false});
            var Q4;
            Q4=makeQuery(id+"F1.opExtrude","CAP_FACE",FACE,{"disambiguationData":[OSD([sQuery(id+"F0.wireOp",EDGE,"E140"),sQuery(id+"F0.wireOp",EDGE,"E141"),sQuery(id+"F0.wireOp",EDGE,"E142"),sQuery(id+"F0.wireOp",EDGE,"E143")])],"isStart":false});
            chamfer(context, id + "F3", {"entities" : qUnion([Q0, Q1, Q2, Q3, Q4]), "width" : .1 * mm, "tangentPropagation" : true});
        }
        {
            var Q0;
            Q0=makeQuery(id+"F1.opExtrude","SWEPT_BODY",BODY,{"disambiguationData":[OSD([sQuery(id+"F0.wireOp",EDGE,"E0.right"),sQuery(id+"F0.wireOp",EDGE,"E3")])]});
            deleteBodies(context, id + "F4", {"entities" : qUnion([Q0])});
        }
        {
            var Q0;
            Q0=makeQuery(id+"F1.opExtrude","CAP_FACE",FACE,{"disambiguationData":[OSD([sQuery(id+"F0.wireOp",EDGE,"E0.right"),sQuery(id+"F0.wireOp",EDGE,"E3"),sQuery(id+"F0.wireOp",EDGE,"E6.trimOffspring")])],"isStart":true});
            var Q1;
            Q1=makeQuery(id+"F1.opExtrude","CAP_FACE",FACE,{"disambiguationData":[OSD([sQuery(id+"F0.wireOp",EDGE,"E0.bottom"),sQuery(id+"F0.wireOp",EDGE,"E0.left"),sQuery(id+"F0.wireOp",EDGE,"E1")])],"isStart":true});
            var Q2;
            Q2=makeQuery(id+"F1.opExtrude","CAP_FACE",FACE,{"disambiguationData":[OSD([sQuery(id+"F0.wireOp",EDGE,"E0.right"),sQuery(id+"F0.wireOp",EDGE,"E3"),sQuery(id+"F0.wireOp",EDGE,"E4.trimOffspring")])],"isStart":true});
            var Q3;
            Q3=makeQuery(id+"F1.opExtrude","CAP_FACE",FACE,{"disambiguationData":[OSD([sQuery(id+"F0.wireOp",EDGE,"E0.top"),sQuery(id+"F0.wireOp",EDGE,"E2"),sQuery(id+"F0.wireOp",EDGE,"E5.trimOffspring")])],"isStart":true});
            var Q4;
            Q4=makeQuery(id+"F1.opExtrude","CAP_FACE",FACE,{"disambiguationData":[OSD([sQuery(id+"F0.wireOp",EDGE,"E96"),sQuery(id+"F0.wireOp",EDGE,"E97"),sQuery(id+"F0.wireOp",EDGE,"E98"),sQuery(id+"F0.wireOp",EDGE,"E99"),sQuery(id+"F0.wireOp",EDGE,"E100"),sQuery(id+"F0.wireOp",EDGE,"E101"),sQuery(id+"F0.wireOp",EDGE,"E102"),sQuery(id+"F0.wireOp",EDGE,"E103"),sQuery(id+"F0.wireOp",EDGE,"E104"),sQuery(id+"F0.wireOp",EDGE,"E105"),sQuery(id+"F0.wireOp",EDGE,"E106"),sQuery(id+"F0.wireOp",EDGE,"E107"),sQuery(id+"F0.wireOp",EDGE,"E108"),sQuery(id+"F0.wireOp",EDGE,"E109"),sQuery(id+"F0.wireOp",EDGE,"E110"),sQuery(id+"F0.wireOp",EDGE,"E111"),sQuery(id+"F0.wireOp",EDGE,"E112"),sQuery(id+"F0.wireOp",EDGE,"E113")])],"isStart":true});
            var Q5;
            Q5=makeQuery(id+"F1.opExtrude","CAP_FACE",FACE,{"disambiguationData":[OSD([sQuery(id+"F0.wireOp",EDGE,"E88"),sQuery(id+"F0.wireOp",EDGE,"E89"),sQuery(id+"F0.wireOp",EDGE,"E90"),sQuery(id+"F0.wireOp",EDGE,"E91"),sQuery(id+"F0.wireOp",EDGE,"E92"),sQuery(id+"F0.wireOp",EDGE,"E93"),sQuery(id+"F0.wireOp",EDGE,"E94"),sQuery(id+"F0.wireOp",EDGE,"E95")])],"isStart":true});
            var Q6;
            Q6=makeQuery(id+"F1.opExtrude","CAP_FACE",FACE,{"disambiguationData":[OSD([sQuery(id+"F0.wireOp",EDGE,"E71"),sQuery(id+"F0.wireOp",EDGE,"E72"),sQuery(id+"F0.wireOp",EDGE,"E73"),sQuery(id+"F0.wireOp",EDGE,"E74"),sQuery(id+"F0.wireOp",EDGE,"E75"),sQuery(id+"F0.wireOp",EDGE,"E76"),sQuery(id+"F0.wireOp",EDGE,"E77"),sQuery(id+"F0.wireOp",EDGE,"E78"),sQuery(id+"F0.wireOp",EDGE,"E79"),sQuery(id+"F0.wireOp",EDGE,"E80"),sQuery(id+"F0.wireOp",EDGE,"E81"),sQuery(id+"F0.wireOp",EDGE,"E82"),sQuery(id+"F0.wireOp",EDGE,"E83"),sQuery(id+"F0.wireOp",EDGE,"E84"),sQuery(id+"F0.wireOp",EDGE,"E85"),sQuery(id+"F0.wireOp",EDGE,"E86"),sQuery(id+"F0.wireOp",EDGE,"E87")])],"isStart":true});
            var Q7;
            Q7=makeQuery(id+"F1.opExtrude","CAP_FACE",FACE,{"disambiguationData":[OSD([sQuery(id+"F0.wireOp",EDGE,"E45"),sQuery(id+"F0.wireOp",EDGE,"E46"),sQuery(id+"F0.wireOp",EDGE,"E47"),sQuery(id+"F0.wireOp",EDGE,"E48"),sQuery(id+"F0.wireOp",EDGE,"E49"),sQuery(id+"F0.wireOp",EDGE,"E50"),sQuery(id+"F0.wireOp",EDGE,"E51"),sQuery(id+"F0.wireOp",EDGE,"E52"),sQuery(id+"F0.wireOp",EDGE,"E53"),sQuery(id+"F0.wireOp",EDGE,"E54"),sQuery(id+"F0.wireOp",EDGE,"E55"),sQuery(id+"F0.wireOp",EDGE,"E56"),sQuery(id+"F0.wireOp",EDGE,"E57"),sQuery(id+"F0.wireOp",EDGE,"E58"),sQuery(id+"F0.wireOp",EDGE,"E59"),sQuery(id+"F0.wireOp",EDGE,"E60"),sQuery(id+"F0.wireOp",EDGE,"E61"),sQuery(id+"F0.wireOp",EDGE,"E62"),sQuery(id+"F0.wireOp",EDGE,"E63"),sQuery(id+"F0.wireOp",EDGE,"E64"),sQuery(id+"F0.wireOp",EDGE,"E65"),sQuery(id+"F0.wireOp",EDGE,"E66"),sQuery(id+"F0.wireOp",EDGE,"E67"),sQuery(id+"F0.wireOp",EDGE,"E68"),sQuery(id+"F0.wireOp",EDGE,"E69"),sQuery(id+"F0.wireOp",EDGE,"E70")])],"isStart":true});
            var Q8;
            Q8=makeQuery(id+"F1.opExtrude","CAP_FACE",FACE,{"disambiguationData":[OSD([sQuery(id+"F0.wireOp",EDGE,"E9"),sQuery(id+"F0.wireOp",EDGE,"E10"),sQuery(id+"F0.wireOp",EDGE,"E11"),sQuery(id+"F0.wireOp",EDGE,"E12"),sQuery(id+"F0.wireOp",EDGE,"E13"),sQuery(id+"F0.wireOp",EDGE,"E14"),sQuery(id+"F0.wireOp",EDGE,"E15"),sQuery(id+"F0.wireOp",EDGE,"E16"),sQuery(id+"F0.wireOp",EDGE,"E17"),sQuery(id+"F0.wireOp",EDGE,"E18"),sQuery(id+"F0.wireOp",EDGE,"E19"),sQuery(id+"F0.wireOp",EDGE,"E20"),sQuery(id+"F0.wireOp",EDGE,"E22"),sQuery(id+"F0.wireOp",EDGE,"E23"),sQuery(id+"F0.wireOp",EDGE,"E24"),sQuery(id+"F0.wireOp",EDGE,"E25"),sQuery(id+"F0.wireOp",EDGE,"E26"),sQuery(id+"F0.wireOp",EDGE,"E27"),sQuery(id+"F0.wireOp",EDGE,"E28"),sQuery(id+"F0.wireOp",EDGE,"E29"),sQuery(id+"F0.wireOp",EDGE,"E30"),sQuery(id+"F0.wireOp",EDGE,"E31"),sQuery(id+"F0.wireOp",EDGE,"E32"),sQuery(id+"F0.wireOp",EDGE,"E33"),sQuery(id+"F0.wireOp",EDGE,"E34"),sQuery(id+"F0.wireOp",EDGE,"E35"),sQuery(id+"F0.wireOp",EDGE,"E36"),sQuery(id+"F0.wireOp",EDGE,"E37"),sQuery(id+"F0.wireOp",EDGE,"E38"),sQuery(id+"F0.wireOp",EDGE,"E39"),sQuery(id+"F0.wireOp",EDGE,"E40"),sQuery(id+"F0.wireOp",EDGE,"E41"),sQuery(id+"F0.wireOp",EDGE,"E42"),sQuery(id+"F0.wireOp",EDGE,"E43"),sQuery(id+"F0.wireOp",EDGE,"E44")])],"isStart":true});
            var Q9;
            Q9=makeQuery(id+"F1.opExtrude","CAP_FACE",FACE,{"disambiguationData":[OSD([sQuery(id+"F0.wireOp",EDGE,"E8")])],"isStart":true});
            fillet(context, id + "F5", {"entities" : qUnion([Q0, Q1, Q2, Q3, Q4, Q5, Q6, Q7, Q8, Q9]), "radius" : .1 * mm, "tangentPropagation" : true, "allowEdgeOverflow" : false});
        }
        {
            var Q0;
            Q0=makeQuery(id+"F1.opExtrude","CAP_FACE",FACE,{"disambiguationData":[OSD([sQuery(id+"F0.wireOp",EDGE,"E140"),sQuery(id+"F0.wireOp",EDGE,"E141"),sQuery(id+"F0.wireOp",EDGE,"E142"),sQuery(id+"F0.wireOp",EDGE,"E143")])],"isStart":true});
            var Q1;
            Q1=makeQuery(id+"F1.opExtrude","CAP_FACE",FACE,{"disambiguationData":[OSD([sQuery(id+"F0.wireOp",EDGE,"E136.bottom"),sQuery(id+"F0.wireOp",EDGE,"E136.top"),sQuery(id+"F0.wireOp",EDGE,"E136.left"),sQuery(id+"F0.wireOp",EDGE,"E136.right"),sQuery(id+"F0.wireOp",EDGE,"E137.bottom"),sQuery(id+"F0.wireOp",EDGE,"E137.top"),sQuery(id+"F0.wireOp",EDGE,"E137.right"),sQuery(id+"F0.wireOp",EDGE,"E138.bottom"),sQuery(id+"F0.wireOp",EDGE,"E138.top"),sQuery(id+"F0.wireOp",EDGE,"E138.right"),sQuery(id+"F0.wireOp",EDGE,"E139.bottom"),sQuery(id+"F0.wireOp",EDGE,"E139.top"),sQuery(id+"F0.wireOp",EDGE,"E139.right")])],"isStart":true});
            var Q2;
            Q2=makeQuery(id+"F1.opExtrude","CAP_FACE",FACE,{"disambiguationData":[OSD([sQuery(id+"F0.wireOp",EDGE,"E125"),sQuery(id+"F0.wireOp",EDGE,"E126"),sQuery(id+"F0.wireOp",EDGE,"E127"),sQuery(id+"F0.wireOp",EDGE,"E128"),sQuery(id+"F0.wireOp",EDGE,"E129"),sQuery(id+"F0.wireOp",EDGE,"E130"),sQuery(id+"F0.wireOp",EDGE,"E131"),sQuery(id+"F0.wireOp",EDGE,"E132"),sQuery(id+"F0.wireOp",EDGE,"E133"),sQuery(id+"F0.wireOp",EDGE,"E134"),sQuery(id+"F0.wireOp",EDGE,"E135")])],"isStart":true});
            var Q3;
            Q3=makeQuery(id+"F1.opExtrude","CAP_FACE",FACE,{"disambiguationData":[OSD([sQuery(id+"F0.wireOp",EDGE,"E117"),sQuery(id+"F0.wireOp",EDGE,"E118"),sQuery(id+"F0.wireOp",EDGE,"E119"),sQuery(id+"F0.wireOp",EDGE,"E120"),sQuery(id+"F0.wireOp",EDGE,"E121"),sQuery(id+"F0.wireOp",EDGE,"E122"),sQuery(id+"F0.wireOp",EDGE,"E123"),sQuery(id+"F0.wireOp",EDGE,"E124")])],"isStart":true});
            var Q4;
            Q4=makeQuery(id+"F1.opExtrude","CAP_FACE",FACE,{"disambiguationData":[OSD([sQuery(id+"F0.wireOp",EDGE,"E114.bottom"),sQuery(id+"F0.wireOp",EDGE,"E114.top"),sQuery(id+"F0.wireOp",EDGE,"E114.left"),sQuery(id+"F0.wireOp",EDGE,"E114.right"),sQuery(id+"F0.wireOp",EDGE,"E115.bottom"),sQuery(id+"F0.wireOp",EDGE,"E115.top"),sQuery(id+"F0.wireOp",EDGE,"E115.left"),sQuery(id+"F0.wireOp",EDGE,"E115.right"),sQuery(id+"F0.wireOp",EDGE,"E116.bottom"),sQuery(id+"F0.wireOp",EDGE,"E116.top")])],"isStart":true});
            chamfer(context, id + "F6", {"entities" : qUnion([Q0, Q1, Q2, Q3, Q4]), "width" : .1 * mm, "tangentPropagation" : true});
        }
    });
